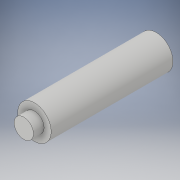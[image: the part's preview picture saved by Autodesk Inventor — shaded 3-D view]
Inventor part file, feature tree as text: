
AUTODESK INVENTOR PART (.ipt)
format: ipt  version: 2018 (Build 220112000, 112)  size: 101,376 bytes
history: native  units: in
note: dims shown in document units (in); Inventor stores cm internally (conversion verified against a paired STEP export)
features: extrude x2, sketch x2
ambient origin geometry x8: Origin, YZ Plane, XZ Plane, XY Plane, X Axis, Y Axis, Z Axis, Center Point
bodies: Solid1 (feature_tree)
feature tree (4):
  extrude  "Extrusion1"  Depth=0.5in
  extrude  "Extrusion2"  Depth=3.4252in
  sketch  "Sketch1"  dims[d0=0.8661in d1=0.5in]
  sketch  "Sketch2"  dims[d2=3.1496in d3=0.0in d4=0.5in d5=3.4252in d6=0.0in]
